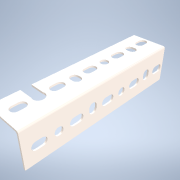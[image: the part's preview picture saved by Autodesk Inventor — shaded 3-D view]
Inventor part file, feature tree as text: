
AUTODESK INVENTOR PART (.ipt)
format: ipt  version: 2021 (Build 250183000, 183)  size: 221,696 bytes
history: mixed  units: in
note: dims shown in document units (in); Inventor stores cm internally (conversion verified against a paired STEP export)
features: extrude x2, sketch x2, other x1, imported_body x1
ambient origin geometry x8: Origin, YZ Plane, XZ Plane, XY Plane, X Axis, Y Axis, Z Axis, Center Point
bodies: Solid1 (imported_parasolid)
feature tree (6):
  other  "Other side cuts"
  extrude  "Extrusion1"  Depth=0.4331in
  extrude  "Extrusion2"  Depth=0.4331in
  sketch  "Sketch1"  dims[d0=0.4724in d1=0.4331in]
  sketch  "Sketch2"  dims[d2=0.0in d3=0.0in d4=0.4724in d5=0.4331in d6=0.0in d7=0.0in d8=0.0197in d9=0.0344in]
  imported_body  NMx_Import_Brep_tag  [imported B-rep: ~80 faces, bbox_mm=[40.1, 40.1, 177.8]]
